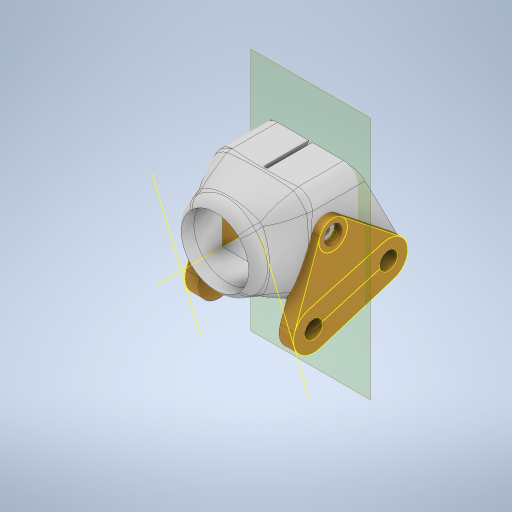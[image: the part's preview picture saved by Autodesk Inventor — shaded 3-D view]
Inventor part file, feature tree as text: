
AUTODESK INVENTOR PART (.ipt)
format: ipt  version: 2023 (Build 270158000, 158)  size: 1,075,200 bytes
history: native  units: in
note: dims shown in document units (in); Inventor stores cm internally (conversion verified against a paired STEP export)
features: sketch x7, other x4, extrude x4, projected_geometry x4, fillet x1, plane x1
ambient origin geometry x8: Origin, YZ Plane, XZ Plane, XY Plane, X Axis, Y Axis, Z Axis, Center Point
bodies: Solid1 (feature_tree)
feature tree (21):
  other  "mini predator camera block for boolian.iam"
  other  "mini predator camera block.ipt:1"
  other  "Kauri modular camera mount mini.ipt:1"
  other  "adjustable camera mount mirror.ipt:1"
  extrude  "Extrusion1"  Depth=0.3937in TaperAngle=0.0deg
  extrude  "Extrusion2"  Depth=1.0in TaperAngle=0.0deg
  extrude  "Extrusion3"  TaperAngle=90.0deg  [1 undecoded]
  fillet  "Fillet1"  Radius=0.0197in
  plane  "Work Plane1"
  extrude  "Extrusion4"  [1 undecoded]
  sketch  "Sketch18"
  sketch  "Sketch2"  dims[d3=1.0in d4=0.0in d5=1.0in d6=0.0in]
  sketch  "Sketch2_1"  dims[d0=0.3937in d1=1.0in d2=0.0in]
  sketch  "Sketch4"  dims[d7=0.125in d8=90.0deg d9=0.0197in]
  projected_geometry  "Projected Loop1"
  projected_geometry  "Projected Loop2"
  sketch  "Sketch5"  dims[d10=0.5in d11=0.0in]
  sketch  "Sketch6"
  projected_geometry  "Projected Loop3"
  projected_geometry  "Projected Loop4"
  sketch  "Sketch7"
note: 2 required parameter values undecoded (feature->parameter linkage not recoverable at this tier; creation-order binding heuristic only, values carry confidence <= 0.55)
